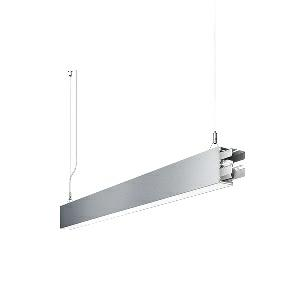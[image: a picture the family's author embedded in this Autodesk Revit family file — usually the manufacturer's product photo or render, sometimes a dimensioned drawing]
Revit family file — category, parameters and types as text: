
# Revit family: idoo_line_-_ilp_3000_vtl_d_sta_00806465_11b3
name_source: partatom
category: Lighting Fixtures
units: mm (PartAtom-declared; Revit-internal decimal feet)

## family parameters
Cut with Voids When Loaded = No
Host = Face
Light Source = No
Part Type = Normal
Room Calculation Point = No
Round Connector Dimension = Use Diameter
Shared = No

## types (1)
- IDOO.line - ILP 3000/VTL/D STA (1 x LED, 3150 lm, 2700-6500K)
    Apparent Load = 32 VA
    Approval mark = CE
    CIE Flux Codes = 66 91 98 40 100
    Color Rendering = 90-100
    Color Temperature = 2700-6500K
    Control Gear = Electronic ballast
    Default Elevation = 1800 mm
    Description = ILP 3000/VTL/D|Suspended luminaire|light source: LED|connected load: 220-240 V, 50/60 Hz|Power consumption: approx. 32 W|standby: approx. 0,25|luminous flux: 3150 lm|luminous efficacy: 98 lm/W|light distribution: Direct/indirect|direct ratio: approx. 40 %|colour temperature: Cold white, ca. 2700-6500 K|color rendering index (CRI): >= 90|chromaticity tolerance:  3 SDCM|System of protection: IP 40|technology: Continuously dimmable|luminaire body|material: Sectional aluminium|colour: Silver|lamp cover: Acrylic (PMMA), Clear|mains lead: 2.00 m With free stranded wires|Fastening: Steel cable 0.3 - 0.7 m|glare control: Prism aperture|luminance(L65): <= 2700 cd/m|unified glare rating(4H 8H): <=  16|special features: Specified values at approx. 4000 K, DALI Load 1x, Through-wired, up to 18 m on one mains connection, External control required for Dali Device type 8, Flicker-free, Constant luminous flux between 2700 and 6500 K, Constant colour temperature over the whole dimming range, Suitable as emergency lighting, Start luminaire with mains connection, Mechanical and electrical connection of the individual modules without tools|
    Frequency = 50 Hz
    Height = 110 mm
    Lamp = 1 x LED
    Lamp Light Flux = 3150 lm
    Lamp count = 1
    Length = 1128 mm
    Luminous efficacy = 98 lm/W
    Manufacturer = Waldmann
    ModVariant = No
    Model = 00806465
    Mounting Place = Ceiling
    Mounting Type = Pendant
    Number of Poles = 1
    OnlyDefault = Yes
    Power Factor = 1
    Product Name = IDOO.line - ILP 3000/VTL/D STA
    Product group = Suspended luminaire
    ProductGroupID = 9
    Protection Class = Protection class I
    Protection Degree = IP 40
    RLX_Detail_Level = 1
    RLX_Emergency_Light_Flux = 0 lm
    RLX_Emergency_Type = 0
    RLX_Emergency_Type_DB = No
    RlxData = <blob elided: 22685 chars, md5=46e76d5e>
    Socket = socket
    Standby Power = 0 W
    System Light Flux = 3150 lm
    System Power = 32 W
    Type Comments = Product without accessories
    Type Image = 113304000-00692576.jpg
    URL = http://relux.com
    VarID = ---
    Voltage = 230 V
    Voltage Range = 220-240 V
    Weight = 0.00 kg
    Width = 60 mm  [stored 0.19685 ft]

note: [stored X ft] marks values corroborated as IEEE doubles in the binary element streams (Revit-internal decimal feet)

## geometry (parser evidence)
native form markers: Blend x4, Sweep x13
no freeform markers — native parametric forms only
